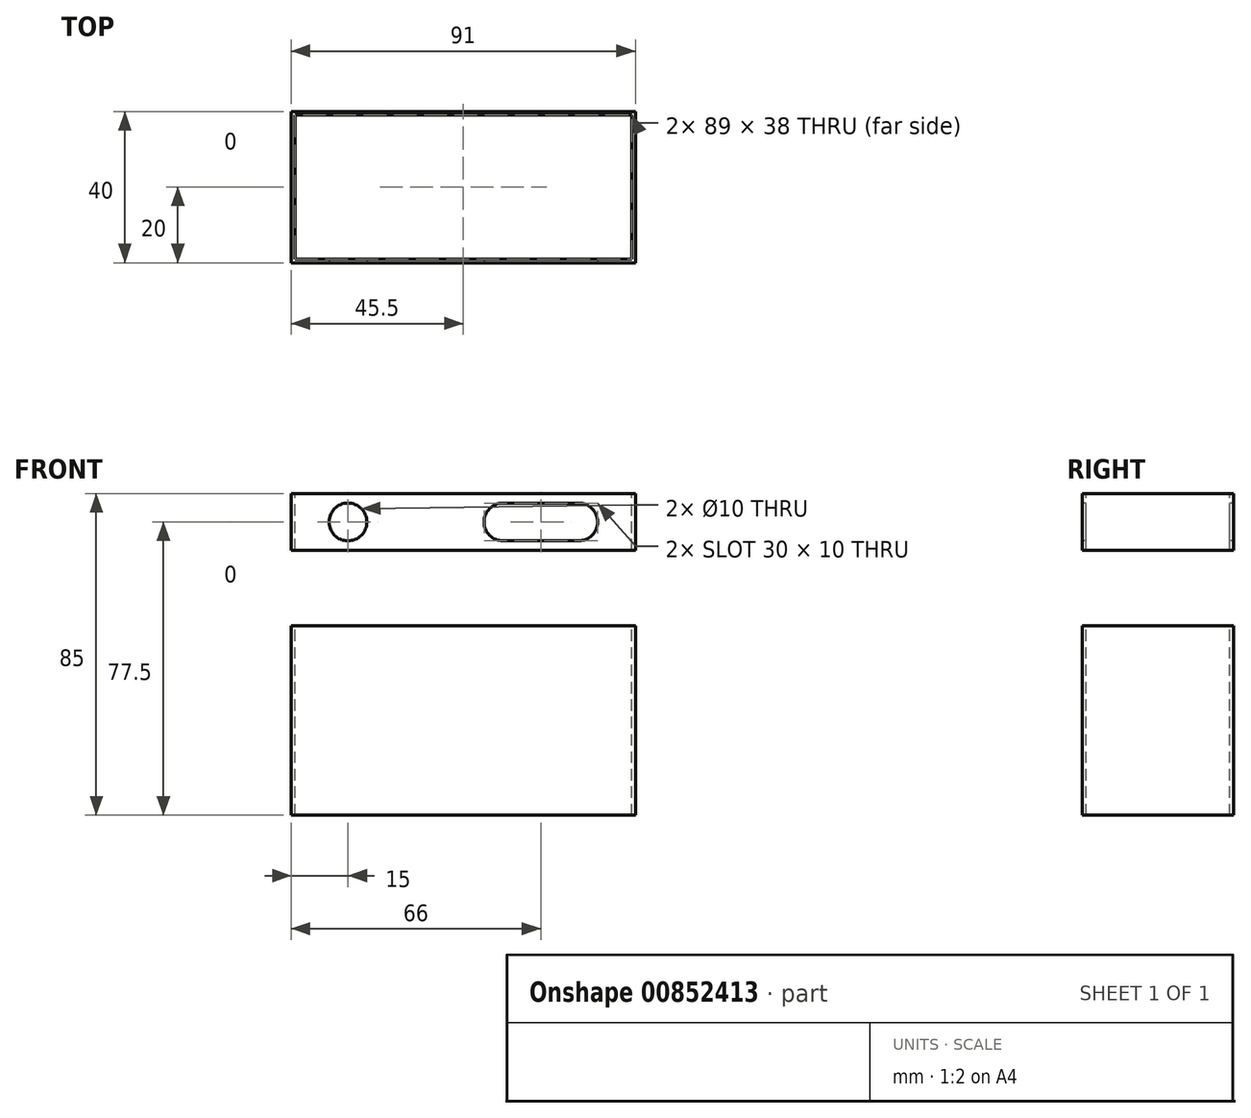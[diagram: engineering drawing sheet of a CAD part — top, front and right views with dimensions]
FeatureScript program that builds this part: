
annotation { "Feature Type Name" : "Feature", "Feature Type Description" : "" }
export const myFeature = defineFeature(function(context is Context, id is Id, definition is map)
    precondition{}
    {
        {
            var Q0;
            Q0=qCreatedBy(makeId("Top.planeOp"),FACE);
            var sketch = newSketch(context, id + "F0", { "sketchPlane" : qUnion([Q0])});
            skLineSegment(sketch, "E0.bottom", {"start": v(0, 0) * mm, "end": v(91, 0) * mm});
            skLineSegment(sketch, "E0.top", {"start": v(0, 40) * mm, "end": v(91, 40) * mm});
            skLineSegment(sketch, "E0.left", {"start": v(0, 0) * mm, "end": v(0, 40) * mm});
            skLineSegment(sketch, "E0.right", {"start": v(91, 0) * mm, "end": v(91, 40) * mm});
            skSolve(sketch);
        }
        {
            var Q0;
            Q0 = qSketchRegion(id + "F0", true);
            extrude(context, id + "F1", {"entities" : qUnion([Q0]), "depth" : 25 * mm, "offsetDistance" : 25 * mm});
        }
        {
            var Q0;
            Q0=makeQuery(id+"F1.opExtrude","CAP_FACE",FACE,{"disambiguationData":[OSD([sQuery(id+"F0.wireOp",EDGE,"E0.bottom"),sQuery(id+"F0.wireOp",EDGE,"E0.top"),sQuery(id+"F0.wireOp",EDGE,"E0.left"),sQuery(id+"F0.wireOp",EDGE,"E0.right")])],"isStart":false});
            var sketch = newSketch(context, id + "F2", { "sketchPlane" : qUnion([Q0])});
            skLineSegment(sketch, "E1.bottom", {"start": v(1, 1) * mm, "end": v(90, 1) * mm});
            skLineSegment(sketch, "E1.top", {"start": v(1, 39) * mm, "end": v(90, 39) * mm});
            skLineSegment(sketch, "E1.left", {"start": v(1, 1) * mm, "end": v(1, 39) * mm});
            skLineSegment(sketch, "E1.right", {"start": v(90, 1) * mm, "end": v(90, 39) * mm});
            skSolve(sketch);
        }
        {
            var Q0;
            Q0 = qSketchRegion(id + "F2", true);
            extrude(context, id + "F3", {"entities" : qUnion([Q0]), "operationType" : NewBodyOperationType.REMOVE, "oppositeDirection" : true, "depth" : 25 * mm, "offsetDistance" : 25 * mm});
        }
        {
            var Q0;
            Q0=qCreatedBy(makeId("Top.planeOp"),FACE);
            var sketch = newSketch(context, id + "F4", { "sketchPlane" : qUnion([Q0])});
            skLineSegment(sketch, "E2.0.0", {"start": v(0, 40) * mm, "end": v(91, 40) * mm});
            skLineSegment(sketch, "E2.0.1", {"start": v(91, 40) * mm, "end": v(91, 0) * mm});
            skLineSegment(sketch, "E2.0.2", {"start": v(91, 0) * mm, "end": v(0, 0) * mm});
            skLineSegment(sketch, "E2.0.3", {"start": v(0, 0) * mm, "end": v(0, 40) * mm});
            skLineSegment(sketch, "E3.0", {"start": v(1, 1) * mm, "end": v(90, 1) * mm});
            skLineSegment(sketch, "E4.0", {"start": v(90, 1) * mm, "end": v(90, 39) * mm});
            skLineSegment(sketch, "E5.0", {"start": v(1, 39) * mm, "end": v(90, 39) * mm});
            skLineSegment(sketch, "E6.0", {"start": v(1, 1) * mm, "end": v(1, 39) * mm});
            skSolve(sketch);
        }
        {
            var Q0;
            Q0 = qSketchRegion(id + "F4", true);
            extrude(context, id + "F5", {"entities" : qUnion([Q0]), "operationType" : NewBodyOperationType.ADD, "oppositeDirection" : true, "depth" : 25 * mm, "offsetDistance" : 25 * mm});
        }
        {
            var Q0;
            Q0=qCreatedBy(makeId("Top.planeOp"),FACE);
            cPlane(context, id + "F6", {"entities" : qUnion([Q0]), "cplaneType" : CPlaneType.OFFSET, "offset" : 60 * mm, "width" : 150 * mm, "height" : 150 * mm});
        }
        {
            var Q0;
            Q0=qCreatedBy(id+"F6.planeOp",FACE);
            var sketch = newSketch(context, id + "F7", { "sketchPlane" : qUnion([Q0])});
            skLineSegment(sketch, "E7.0", {"start": v(0, 0) * mm, "end": v(91, 0) * mm});
            skLineSegment(sketch, "E7.1", {"start": v(0, 40) * mm, "end": v(91, 40) * mm});
            skLineSegment(sketch, "E7.2", {"start": v(0, 0) * mm, "end": v(0, 40) * mm});
            skLineSegment(sketch, "E7.3", {"start": v(91, 0) * mm, "end": v(91, 40) * mm});
            skLineSegment(sketch, "E8.0", {"start": v(1, 1) * mm, "end": v(90, 1) * mm});
            skLineSegment(sketch, "E8.1", {"start": v(1, 39) * mm, "end": v(90, 39) * mm});
            skLineSegment(sketch, "E8.2", {"start": v(1, 1) * mm, "end": v(1, 39) * mm});
            skLineSegment(sketch, "E8.3", {"start": v(90, 1) * mm, "end": v(90, 39) * mm});
            skSolve(sketch);
        }
        {
            var Q0;
            Q0 = qSketchRegion(id + "F7", true);
            extrude(context, id + "F8", {"entities" : qUnion([Q0]), "oppositeDirection" : true, "depth" : 15 * mm, "offsetDistance" : 25 * mm});
        }
        {
            var Q0;
            Q0=makeQuery(id+"F8.opExtrude","SWEPT_FACE",FACE,{"disambiguationData":[OSD([sQuery(id+"F7.wireOp",EDGE,"E7.0")])]});
            var sketch = newSketch(context, id + "F9", { "sketchPlane" : qUnion([Q0])});
            skCircle(sketch, "E9", {"center": v(15, 52.5) * mm, "radius": 5 * mm});
            skLineSegment(sketch, "E10.bottom", {"start": v(56, 57.5) * mm, "end": v(76, 57.5) * mm});
            skLineSegment(sketch, "E10.top", {"start": v(56, 47.5) * mm, "end": v(76, 47.5) * mm});
            skArc(sketch, "E11", {"start": v(76, 47.5) * mm, "mid": v(81, 52.5) * mm, "end": v(76, 57.5) * mm});
            skArc(sketch, "E12", {"start": v(56, 57.5) * mm, "mid": v(51, 52.5) * mm, "end": v(56, 47.5) * mm});
            skSolve(sketch);
        }
        {
            var Q0;
            Q0 = qSketchRegion(id + "F9", true);
            extrude(context, id + "F10", {"entities" : qUnion([Q0]), "operationType" : NewBodyOperationType.REMOVE, "endBound" : BoundingType.THROUGH_ALL, "oppositeDirection" : true, "depth" : 25 * mm, "offsetDistance" : 25 * mm});
        }
    });
